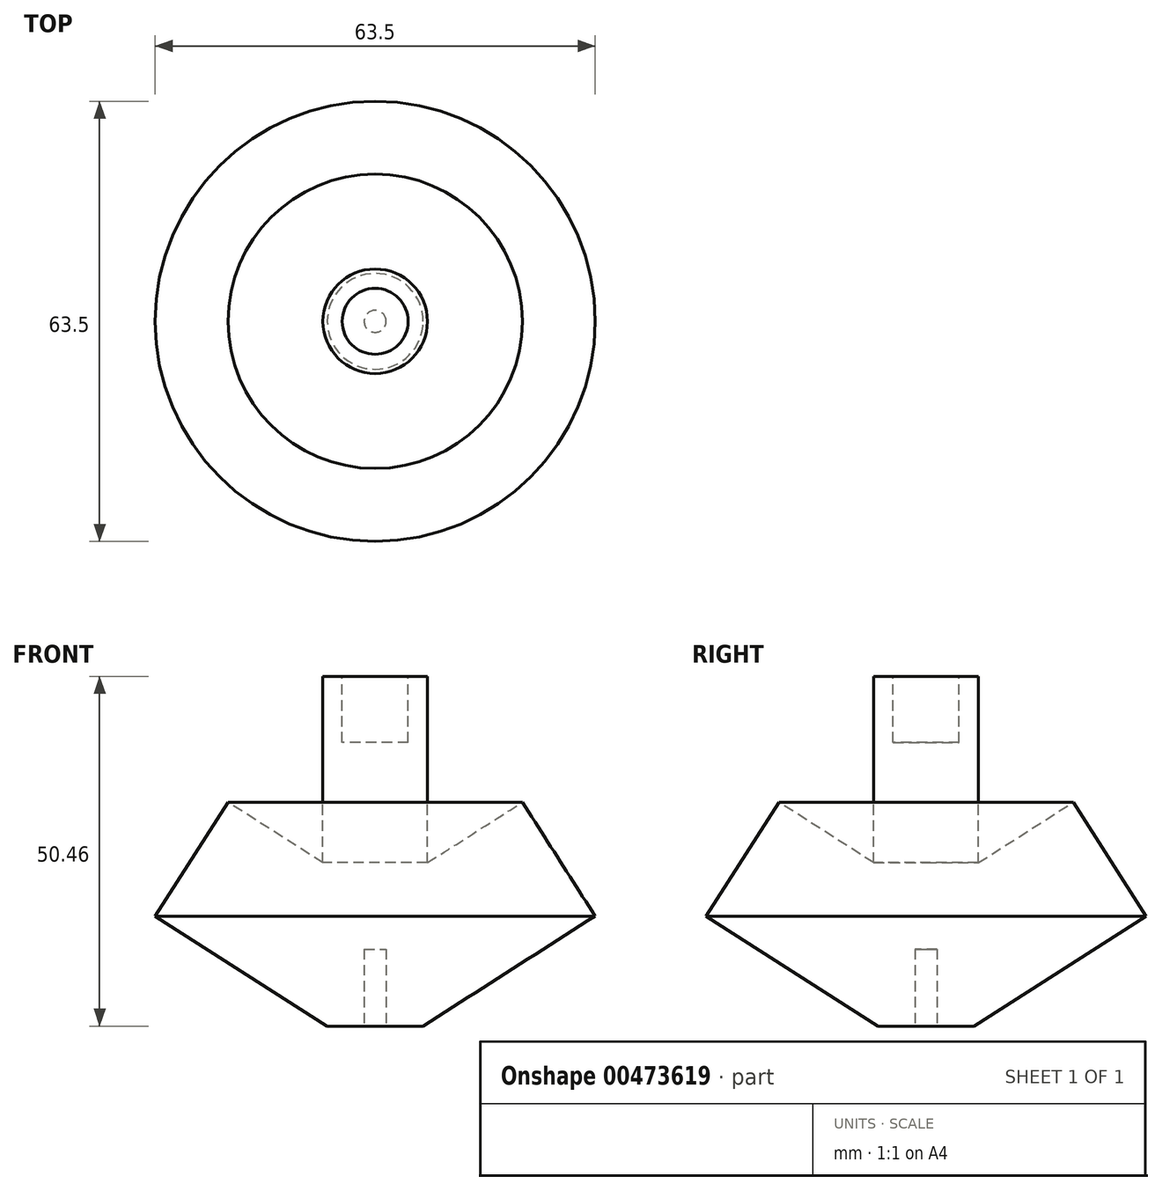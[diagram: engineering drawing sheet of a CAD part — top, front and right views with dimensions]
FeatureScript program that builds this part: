
annotation { "Feature Type Name" : "Feature", "Feature Type Description" : "" }
export const myFeature = defineFeature(function(context is Context, id is Id, definition is map)
    precondition{}
    {
        {
            var Q0;
            Q0=qCreatedBy(makeId("Front.planeOp"),FACE);
            var sketch = newSketch(context, id + "F0", { "sketchPlane" : qUnion([Q0])});
            skLineSegment(sketch, "E0", {"start": v(0, 0) * mm, "end": v(6.92, 0) * mm});
            skLineSegment(sketch, "E1", {"start": v(6.92, 0) * mm, "end": v(31.75, 15.88) * mm});
            skLineSegment(sketch, "E2", {"start": v(31.75, 15.88) * mm, "end": v(21.24, 32.32) * mm});
            skLineSegment(sketch, "E3", {"start": v(21.24, 32.32) * mm, "end": v(7.55, 23.57) * mm});
            skLineSegment(sketch, "E4", {"start": v(7.55, 23.57) * mm, "end": v(7.55, 50.46) * mm});
            skLineSegment(sketch, "E5", {"start": v(7.55, 50.46) * mm, "end": v(0, 50.46) * mm});
            skLineSegment(sketch, "E6", {"start": v(0, 50.46) * mm, "end": v(0, 0) * mm});
            skSolve(sketch);
        }
        {
            var Q0;
            Q0=makeQuery(id+"F0.imprint","IMPRINT",FACE,{"disambiguationData":[TD([[makeQuery(id+"F0.imprint","IMPRINT",EDGE,{"derivedFrom":sQuery(id+"F0.wireOp",EDGE,"E0")}),1.0]])]});
            var Q1;
            Q1=sQuery(id+"F0.wireOp",EDGE,"E6");
            revolve(context, id + "F1", {"entities" : qUnion([Q0]), "axis" : qUnion([Q1]), "revolveType" : RevolveType.FULL});
        }
        {
            var Q0;
            Q0=makeQuery(id+"F1.opRevolve","SWEPT_FACE",FACE,{"disambiguationData":[OSD([sQuery(id+"F0.wireOp",EDGE,"E0")])]});
            var sketch = newSketch(context, id + "F2", { "sketchPlane" : qUnion([Q0])});
            skCircle(sketch, "E7", {"center": v(0, 0) * mm, "radius": 1.59 * mm});
            skSolve(sketch);
        }
        {
            var Q0;
            Q0 = qSketchRegion(id + "F2", true);
            extrude(context, id + "F3", {"entities" : qUnion([Q0]), "operationType" : NewBodyOperationType.REMOVE, "oppositeDirection" : true, "depth" : 11.1 * mm});
        }
        {
            var Q0;
            Q0=makeQuery(id+"F1.opRevolve","SWEPT_FACE",FACE,{"disambiguationData":[OSD([sQuery(id+"F0.wireOp",EDGE,"E5")])]});
            var sketch = newSketch(context, id + "F4", { "sketchPlane" : qUnion([Q0])});
            skCircle(sketch, "E8", {"center": v(0, 0) * mm, "radius": 4.76 * mm});
            skSolve(sketch);
        }
        {
            var Q0;
            Q0 = qSketchRegion(id + "F4", true);
            extrude(context, id + "F5", {"entities" : qUnion([Q0]), "operationType" : NewBodyOperationType.REMOVE, "oppositeDirection" : true, "depth" : 9.52 * mm});
        }
    });
